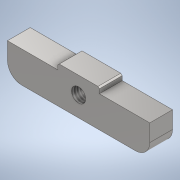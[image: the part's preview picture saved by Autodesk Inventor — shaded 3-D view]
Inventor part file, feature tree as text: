
AUTODESK INVENTOR PART (.ipt)
format: ipt  version: 2020 (Build 240168000, 168)  size: 192,000 bytes
history: native  units: mm
features: other x2, extrude x1
ambient origin geometry x8: Origin, YZ Plane, XZ Plane, XY Plane, X Axis, Y Axis, Z Axis, Center Point
bodies: Body1 (feature_tree)
feature tree (3):
  other  "實體1"
  extrude  "擠出1"  Depth=50.0mm
  other  "螺紋1"
